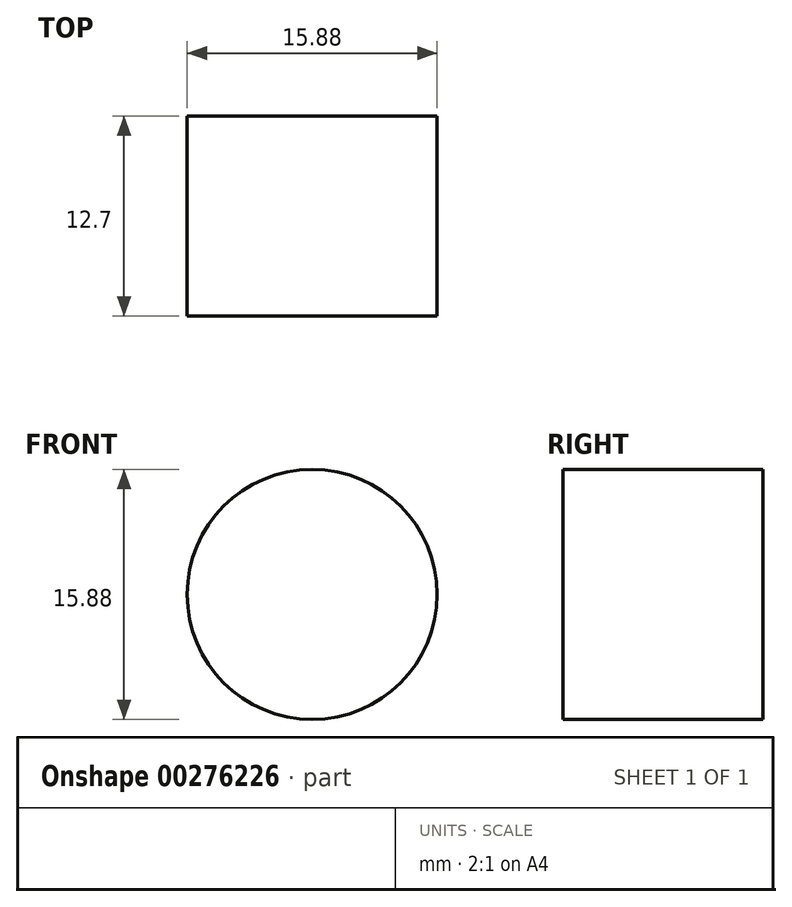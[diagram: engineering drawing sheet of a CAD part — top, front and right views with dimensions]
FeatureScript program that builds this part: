
annotation { "Feature Type Name" : "Feature", "Feature Type Description" : "" }
export const myFeature = defineFeature(function(context is Context, id is Id, definition is map)
    precondition{}
    {
        {
            var Q0;
            Q0=qCreatedBy(makeId("Front.planeOp"),FACE);
            var sketch = newSketch(context, id + "F0", { "sketchPlane" : qUnion([Q0])});
            skLineSegment(sketch, "E0.bottom", {"start": v(0, 0) * mm, "end": v(114.3, 0) * mm});
            skLineSegment(sketch, "E0.top", {"start": v(0, 50.8) * mm, "end": v(114.3, 50.8) * mm});
            skLineSegment(sketch, "E0.left", {"start": v(0, 0) * mm, "end": v(0, 50.8) * mm});
            skLineSegment(sketch, "E0.right", {"start": v(114.3, 0) * mm, "end": v(114.3, 50.8) * mm});
            skLineSegment(sketch, "E1", {"start": v(19.05, 50.8) * mm, "end": v(57.15, 12.7) * mm});
            skLineSegment(sketch, "E2", {"start": v(57.15, 12.7) * mm, "end": v(95.25, 50.8) * mm});
            skLineSegment(sketch, "E3", {"start": v(57.15, 50.8) * mm, "end": v(57.15, 0) * mm, "construction": true});
            skCircle(sketch, "E4", {"center": v(57.15, 50.8) * mm, "radius": 38.1 * mm, "construction": true});
            skSolve(sketch);
        }
        {
            var Q0;
            Q0=makeQuery(id+"F0.imprint","IMPRINT",FACE,{"disambiguationData":[TD([[makeQuery(id+"F0.imprint","IMPRINT",EDGE,{"derivedFrom":sQuery(id+"F0.wireOp",EDGE,"E0.bottom")}),1.0]])]});
            extrude(context, id + "F1", {"entities" : qUnion([Q0]), "depth" : 12.7 * mm});
        }
        {
            var Q0;
            Q0=makeQuery(id+"F1.opExtrude","SWEPT_EDGE",EDGE,{"disambiguationData":[OSD([sQuery(id+"F0.wireOp",EDGE,"E1"),sQuery(id+"F0.wireOp",EDGE,"E2")])]});
            fillet(context, id + "F2", {"entities" : qUnion([Q0]), "radius" : 6.35 * mm, "tangentPropagation" : true, "allowEdgeOverflow" : false});
        }
        {
            var Q0;
            Q0=makeQuery(id+"F1.opExtrude","SWEPT_EDGE",EDGE,{"disambiguationData":[OSD([sQuery(id+"F0.wireOp",EDGE,"E0.top"),sQuery(id+"F0.wireOp",EDGE,"E1")])]});
            var Q1;
            Q1=makeQuery(id+"F1.opExtrude","SWEPT_EDGE",EDGE,{"disambiguationData":[OSD([sQuery(id+"F0.wireOp",EDGE,"E0.top"),sQuery(id+"F0.wireOp",EDGE,"E2")])]});
            fillet(context, id + "F3", {"entities" : qUnion([Q0, Q1]), "radius" : 3.17 * mm, "tangentPropagation" : true, "allowEdgeOverflow" : false});
        }
        {
            var Q0;
            Q0=makeQuery(id+"F1.opExtrude","CAP_FACE",FACE,{"disambiguationData":[OSD([sQuery(id+"F0.wireOp",EDGE,"E0.bottom"),sQuery(id+"F0.wireOp",EDGE,"E0.top"),sQuery(id+"F0.wireOp",EDGE,"E0.left"),sQuery(id+"F0.wireOp",EDGE,"E0.right"),sQuery(id+"F0.wireOp",EDGE,"E1"),sQuery(id+"F0.wireOp",EDGE,"E2")])],"isStart":false});
            var sketch = newSketch(context, id + "F4", { "sketchPlane" : qUnion([Q0])});
            skLineSegment(sketch, "E5.bottom", {"start": v(50.8, 0) * mm, "end": v(63.5, 0) * mm});
            skLineSegment(sketch, "E5.top", {"start": v(50.8, -12.7) * mm, "end": v(63.5, -12.7) * mm});
            skLineSegment(sketch, "E5.left", {"start": v(50.8, 0) * mm, "end": v(50.8, -12.7) * mm});
            skLineSegment(sketch, "E5.right", {"start": v(63.5, 0) * mm, "end": v(63.5, -12.7) * mm});
            skLineSegment(sketch, "E6", {"start": v(57.15, -12.7) * mm, "end": v(57.15, 0) * mm, "construction": true});
            skSolve(sketch);
        }
        {
            var Q0;
            Q0=makeQuery(id+"F4.imprint","IMPRINT",FACE,{"disambiguationData":[TD([[makeQuery(id+"F4.imprint","IMPRINT",EDGE,{"derivedFrom":sQuery(id+"F4.wireOp",EDGE,"E5.bottom")}),-1.0]])]});
            extrude(context, id + "F5", {"entities" : qUnion([Q0]), "operationType" : NewBodyOperationType.ADD, "oppositeDirection" : true, "depth" : 12.7 * mm});
        }
        {
            var Q0;
            Q0=makeQuery(id+"F5.boolean.opBoolean","MERGE",FACE,{"derivedFrom":[makeQuery(id+"F1.opExtrude","CAP_FACE",FACE,{"disambiguationData":[OSD([sQuery(id+"F0.wireOp",EDGE,"E0.bottom"),sQuery(id+"F0.wireOp",EDGE,"E0.top"),sQuery(id+"F0.wireOp",EDGE,"E0.left"),sQuery(id+"F0.wireOp",EDGE,"E0.right"),sQuery(id+"F0.wireOp",EDGE,"E1"),sQuery(id+"F0.wireOp",EDGE,"E2")])],"isStart":false}),makeQuery(id+"F5.opExtrude","CAP_FACE",FACE,{"disambiguationData":[OSD([sQuery(id+"F4.wireOp",EDGE,"E5.bottom"),sQuery(id+"F4.wireOp",EDGE,"E5.top"),sQuery(id+"F4.wireOp",EDGE,"E5.left"),sQuery(id+"F4.wireOp",EDGE,"E5.right")])],"isStart":true})]});
            var sketch = newSketch(context, id + "F6", { "sketchPlane" : qUnion([Q0])});
            skLineSegment(sketch, "E7.bottom", {"start": v(0, 0) * mm, "end": v(19.05, 0) * mm, "construction": true});
            skLineSegment(sketch, "E7.top", {"start": v(0, 19.05) * mm, "end": v(19.05, 19.05) * mm, "construction": true});
            skLineSegment(sketch, "E7.left", {"start": v(0, 0) * mm, "end": v(0, 19.05) * mm, "construction": true});
            skLineSegment(sketch, "E7.right", {"start": v(19.05, 0) * mm, "end": v(19.05, 19.05) * mm, "construction": true});
            skCircle(sketch, "E8", {"center": v(19.05, 19.05) * mm, "radius": 7.94 * mm});
            skLineSegment(sketch, "E9", {"start": v(57.15, 21.68) * mm, "end": v(57.15, -12.7) * mm, "construction": true});
            skCircle(sketch, "E10.MirrorC", {"center": v(95.25, 19.05) * mm, "radius": 7.94 * mm});
            skSolve(sketch);
        }
        {
            var Q0;
            Q0=makeQuery(id+"F6.imprint","IMPRINT",FACE,{"disambiguationData":[TD([[makeQuery(id+"F6.imprint","IMPRINT",EDGE,{"derivedFrom":sQuery(id+"F6.wireOp",EDGE,"E8")}),1.0]])]});
            var Q1;
            Q1=makeQuery(id+"F6.imprint","IMPRINT",FACE,{"disambiguationData":[TD([[makeQuery(id+"F6.imprint","IMPRINT",EDGE,{"derivedFrom":sQuery(id+"F6.wireOp",EDGE,"E10.MirrorC")}),-1.0]])]});
            extrude(context, id + "F7", {"entities" : qUnion([Q0, Q1]), "operationType" : NewBodyOperationType.REMOVE, "oppositeDirection" : true, "depth" : 25.4 * mm});
        }
    });
